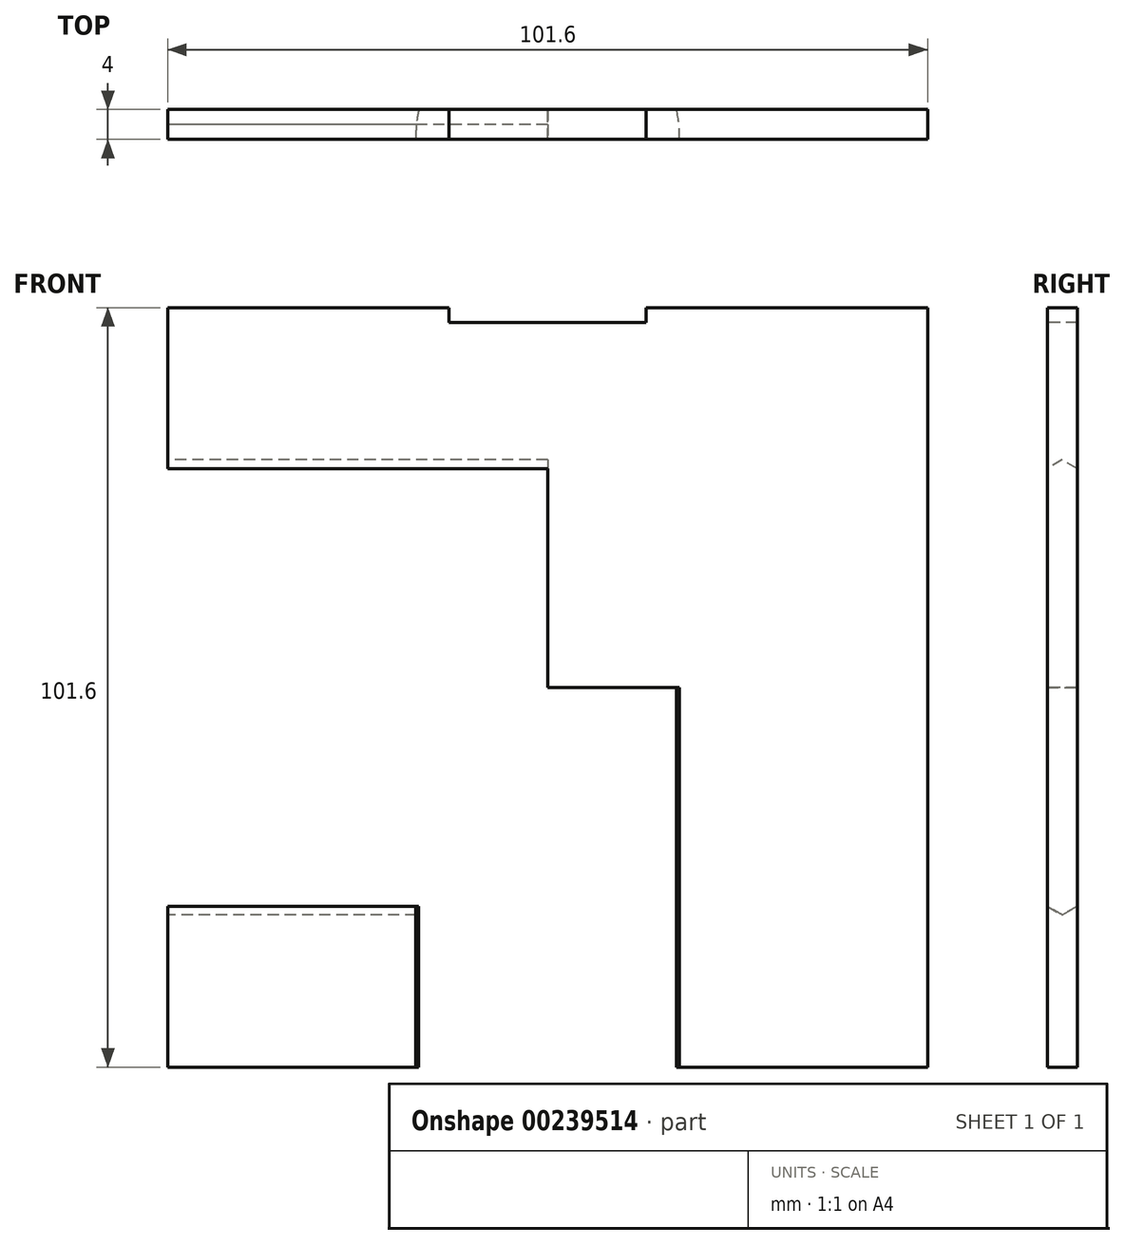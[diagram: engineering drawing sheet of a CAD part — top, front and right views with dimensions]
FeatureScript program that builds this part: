
annotation { "Feature Type Name" : "Feature", "Feature Type Description" : "" }
export const myFeature = defineFeature(function(context is Context, id is Id, definition is map)
    precondition{}
    {
        {
            assignVariable(context, id + "F0", {"name" : "P", "anyValue" : 4});
        }
        {
            var Q0;
            Q0=qCreatedBy(makeId("Front.planeOp"),FACE);
            var sketch = newSketch(context, id + "F1", { "sketchPlane" : qUnion([Q0])});
            skLineSegment(sketch, "E0.bottom", {"start": v(-50.8, 50.8) * mm, "end": v(50.8, 50.8) * mm});
            skLineSegment(sketch, "E0.top", {"start": v(-50.8, -50.8) * mm, "end": v(50.8, -50.8) * mm});
            skLineSegment(sketch, "E0.left", {"start": v(-50.8, 50.8) * mm, "end": v(-50.8, -50.8) * mm});
            skLineSegment(sketch, "E0.right", {"start": v(50.8, 50.8) * mm, "end": v(50.8, -50.8) * mm});
            skPoint(sketch, "E0.middle", {"position": v(0, 0) * mm});
            skSolve(sketch);
        }
        {
            var Q0;
            Q0 = qSketchRegion(id + "F1", true);
            extrude(context, id + "F2", {"entities" : qUnion([Q0]), "endBound" : BoundingType.SYMMETRIC, "depth" : (getVariable(context, 'P')) * mm});
        }
        {
            var Q0;
            Q0=makeQuery(id+"F2.opExtrude","SWEPT_FACE",FACE,{"disambiguationData":[OSD([sQuery(id+"F1.wireOp",EDGE,"E0.bottom")])]});
            var sketch = newSketch(context, id + "F3", { "sketchPlane" : qUnion([Q0])});
            skLineSegment(sketch, "E1.bottom", {"start": v(-13.18, 11.3) * mm, "end": v(13.18, 11.3) * mm});
            skLineSegment(sketch, "E1.top", {"start": v(-13.18, -11.3) * mm, "end": v(13.18, -11.3) * mm});
            skLineSegment(sketch, "E1.left", {"start": v(-13.18, 11.3) * mm, "end": v(-13.18, -11.3) * mm});
            skLineSegment(sketch, "E1.right", {"start": v(13.18, 11.3) * mm, "end": v(13.18, -11.3) * mm});
            skPoint(sketch, "E1.middle", {"position": v(0, 0) * mm});
            skSolve(sketch);
        }
        {
            var Q0;
            Q0 = qSketchRegion(id + "F3", true);
            extrude(context, id + "F4", {"entities" : qUnion([Q0]), "operationType" : NewBodyOperationType.REMOVE, "oppositeDirection" : true, "depth" : (((getVariable(context, 'P')) / 2)) * mm});
        }
        {
            var Q0;
            Q0=makeQuery(id+"F2.opExtrude","SWEPT_FACE",FACE,{"disambiguationData":[OSD([sQuery(id+"F1.wireOp",EDGE,"E0.top")])]});
            var sketch = newSketch(context, id + "F5", { "sketchPlane" : qUnion([Q0])});
            skCircle(sketch, "E2", {"center": v(0, 1.73) * mm, "radius": 17.63 * mm});
            skSolve(sketch);
        }
        {
            var Q0;
            Q0 = qSketchRegion(id + "F5", true);
            extrude(context, id + "F6", {"entities" : qUnion([Q0]), "operationType" : NewBodyOperationType.REMOVE, "oppositeDirection" : true, "depth" : 50.8 * mm});
        }
        {
            var Q0;
            Q0=makeQuery(id+"F2.opExtrude","SWEPT_FACE",FACE,{"disambiguationData":[OSD([sQuery(id+"F1.wireOp",EDGE,"E0.left")])]});
            var sketch = newSketch(context, id + "F7", { "sketchPlane" : qUnion([Q0])});
            skCircle(sketch, "E3.cCircle", {"center": v(0, 0) * mm, "radius": 26.36 * mm, "construction": true});
            skLineSegment(sketch, "E3.0", {"start": v(26.36, 15.22) * mm, "end": v(26.36, -15.22) * mm});
            skLineSegment(sketch, "E3.1", {"start": v(26.36, -15.22) * mm, "end": v(0, -30.44) * mm});
            skLineSegment(sketch, "E3.2", {"start": v(0, -30.44) * mm, "end": v(-26.36, -15.22) * mm});
            skLineSegment(sketch, "E3.3", {"start": v(-26.36, -15.22) * mm, "end": v(-26.36, 15.22) * mm});
            skLineSegment(sketch, "E3.4", {"start": v(-26.36, 15.22) * mm, "end": v(0, 30.44) * mm});
            skLineSegment(sketch, "E3.5", {"start": v(0, 30.44) * mm, "end": v(26.36, 15.22) * mm});
            skPoint(sketch, "E3.0.midPoint", {"position": v(26.36, 0) * mm});
            skSolve(sketch);
        }
        {
            var Q0;
            Q0 = qSketchRegion(id + "F7", true);
            extrude(context, id + "F8", {"entities" : qUnion([Q0]), "operationType" : NewBodyOperationType.REMOVE, "oppositeDirection" : true, "depth" : 50.8 * mm});
        }
    });
